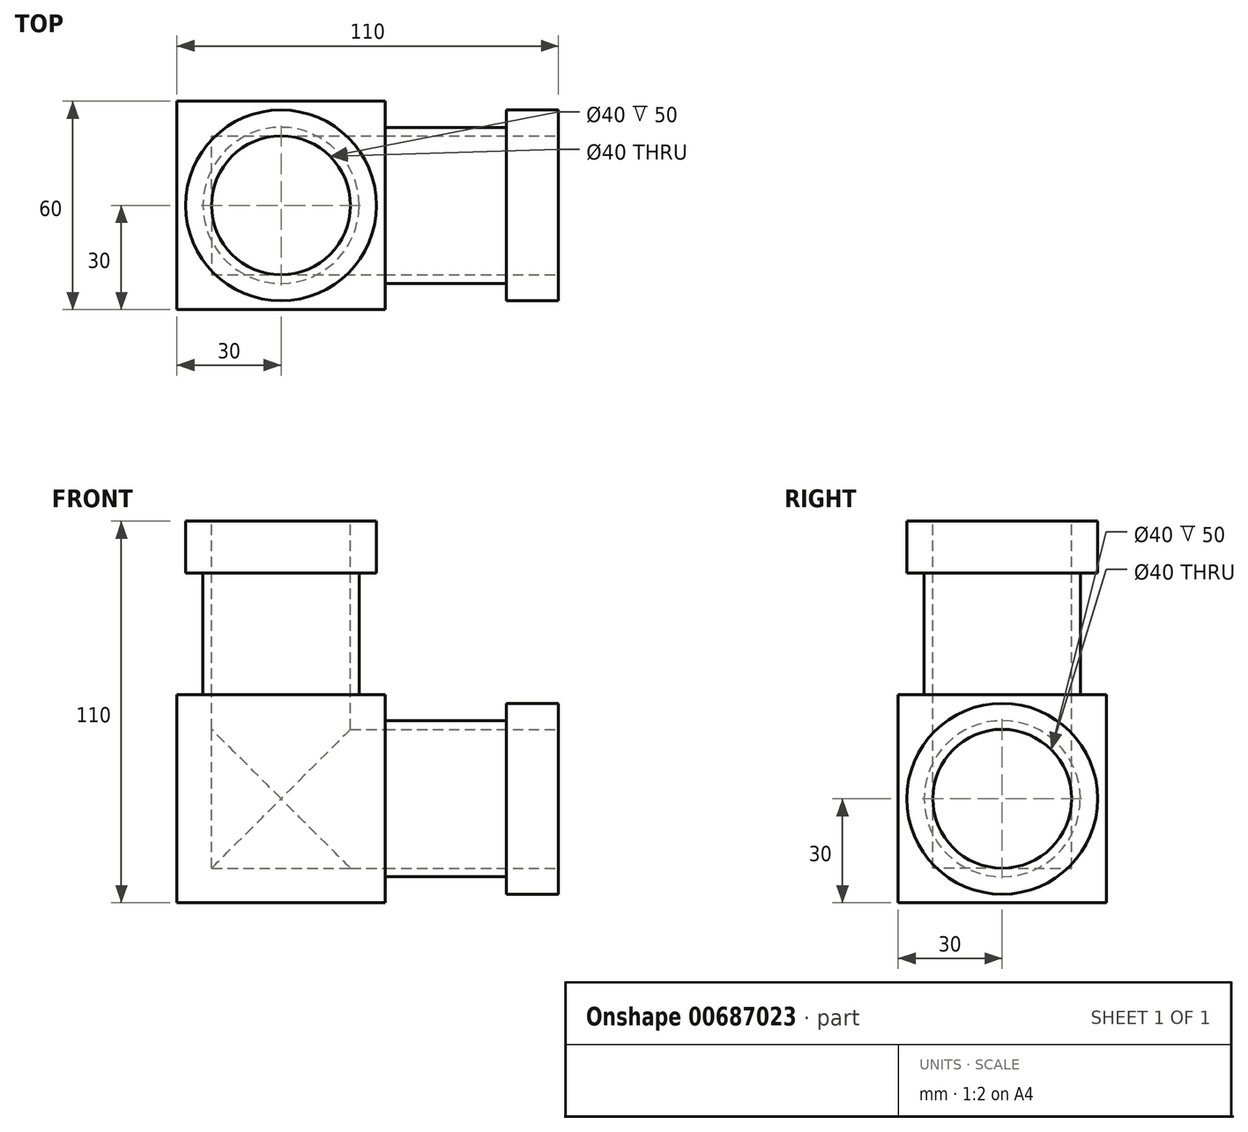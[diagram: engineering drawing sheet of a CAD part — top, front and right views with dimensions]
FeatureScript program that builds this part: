
annotation { "Feature Type Name" : "Feature", "Feature Type Description" : "" }
export const myFeature = defineFeature(function(context is Context, id is Id, definition is map)
    precondition{}
    {
        {
            var Q0;
            Q0=qCreatedBy(makeId("Top.planeOp"),FACE);
            var sketch = newSketch(context, id + "F0", { "sketchPlane" : qUnion([Q0])});
            skLineSegment(sketch, "E0.bottom", {"start": v(30, 30) * mm, "end": v(-30, 30) * mm});
            skLineSegment(sketch, "E0.top", {"start": v(30, -30) * mm, "end": v(-30, -30) * mm});
            skLineSegment(sketch, "E0.left", {"start": v(30, 30) * mm, "end": v(30, -30) * mm});
            skLineSegment(sketch, "E0.right", {"start": v(-30, 30) * mm, "end": v(-30, -30) * mm});
            skPoint(sketch, "E0.middle", {"position": v(0, 0) * mm});
            skSolve(sketch);
        }
        {
            var Q0;
            Q0 = qSketchRegion(id + "F0", true);
            extrude(context, id + "F1", {"entities" : qUnion([Q0]), "endBound" : BoundingType.SYMMETRIC, "depth" : 60 * mm, "offsetDistance" : 25 * mm});
        }
        {
            var Q0;
            Q0=makeQuery(id+"F1.opExtrude","CAP_FACE",FACE,{"disambiguationData":[OSD([sQuery(id+"F0.wireOp",EDGE,"E0.bottom"),sQuery(id+"F0.wireOp",EDGE,"E0.top"),sQuery(id+"F0.wireOp",EDGE,"E0.left"),sQuery(id+"F0.wireOp",EDGE,"E0.right")])],"isStart":false});
            var sketch = newSketch(context, id + "F2", { "sketchPlane" : qUnion([Q0])});
            skCircle(sketch, "E1", {"center": v(0, 0) * mm, "radius": 22.5 * mm});
            skSolve(sketch);
        }
        {
            var Q0;
            Q0=makeQuery(id+"F2.imprint","IMPRINT",FACE,{"disambiguationData":[TD([[makeQuery(id+"F2.imprint","IMPRINT",EDGE,{"derivedFrom":sQuery(id+"F2.wireOp",EDGE,"E1")}),1.0]])]});
            extrude(context, id + "F3", {"entities" : qUnion([Q0]), "depth" : 35 * mm, "offsetDistance" : 25 * mm});
        }
        {
            var Q0;
            Q0=makeQuery(id+"F3.opExtrude","CAP_FACE",FACE,{"disambiguationData":[OSD([sQuery(id+"F2.wireOp",EDGE,"E1")])],"isStart":false});
            var sketch = newSketch(context, id + "F4", { "sketchPlane" : qUnion([Q0])});
            skCircle(sketch, "E2", {"center": v(0, 0) * mm, "radius": 27.5 * mm});
            skSolve(sketch);
        }
        {
            var Q0;
            Q0 = qSketchRegion(id + "F4", true);
            extrude(context, id + "F5", {"entities" : qUnion([Q0]), "operationType" : NewBodyOperationType.ADD, "depth" : 15 * mm, "offsetDistance" : 25 * mm});
        }
        {
            var Q0;
            Q0=makeQuery(id+"F5.opExtrude","CAP_FACE",FACE,{"disambiguationData":[OSD([sQuery(id+"F4.wireOp",EDGE,"E2")])],"isStart":false});
            var sketch = newSketch(context, id + "F6", { "sketchPlane" : qUnion([Q0])});
            skCircle(sketch, "E3", {"center": v(0, 0) * mm, "radius": 20 * mm});
            skSolve(sketch);
        }
        {
            var Q0;
            Q0=qCreatedBy(makeId("Top.planeOp"),FACE);
            var sketch = newSketch(context, id + "F7", { "sketchPlane" : qUnion([Q0])});
            skLineSegment(sketch, "E4", {"start": v(0, 0) * mm, "end": v(0, 30) * mm, "construction": true});
            skSolve(sketch);
        }
        {
            var Q0;
            Q0=makeQuery(id+"F5.opExtrude","SWEPT_BODY",BODY,{"disambiguationData":[OSD([sQuery(id+"F4.wireOp",EDGE,"E2")])]});
            var Q1;
            Q1=makeQuery(id+"F3.opExtrude","SWEPT_BODY",BODY,{"disambiguationData":[OSD([sQuery(id+"F2.wireOp",EDGE,"E1")])]});
            var Q2;
            Q2=sQuery(id+"F7.wireOp",EDGE,"E4");
            circularPattern(context, id + "F8", {"entities" : qUnion([Q0, Q1]), "axis" : qUnion([Q2]), "angle" : 90 * degree, "instanceCount" : 2, "equalSpace" : true});
        }
        {
            var Q0;
            Q0=makeQuery(id+"F6.imprint","IMPRINT",FACE,{"disambiguationData":[TD([[makeQuery(id+"F6.imprint","IMPRINT",EDGE,{"derivedFrom":sQuery(id+"F6.wireOp",EDGE,"E3")}),1.0]])]});
            extrude(context, id + "F9", {"entities" : qUnion([Q0]), "operationType" : NewBodyOperationType.REMOVE, "oppositeDirection" : true, "depth" : 100 * mm, "offsetDistance" : 25 * mm});
        }
        {
            var Q0;
            Q0=makeQuery(id+"F8.opPattern","COPY",FACE,{"derivedFrom":makeQuery(id+"F5.opExtrude","CAP_FACE",FACE,{"disambiguationData":[OSD([sQuery(id+"F4.wireOp",EDGE,"E2")])],"isStart":false}),"instanceName":"1"});
            var sketch = newSketch(context, id + "F10", { "sketchPlane" : qUnion([Q0])});
            skCircle(sketch, "E5", {"center": v(0, 0) * mm, "radius": 20 * mm});
            skSolve(sketch);
        }
        {
            var Q0;
            Q0 = qSketchRegion(id + "F10", true);
            extrude(context, id + "F11", {"entities" : qUnion([Q0]), "operationType" : NewBodyOperationType.REMOVE, "oppositeDirection" : true, "depth" : 100 * mm, "offsetDistance" : 25 * mm});
        }
    });
